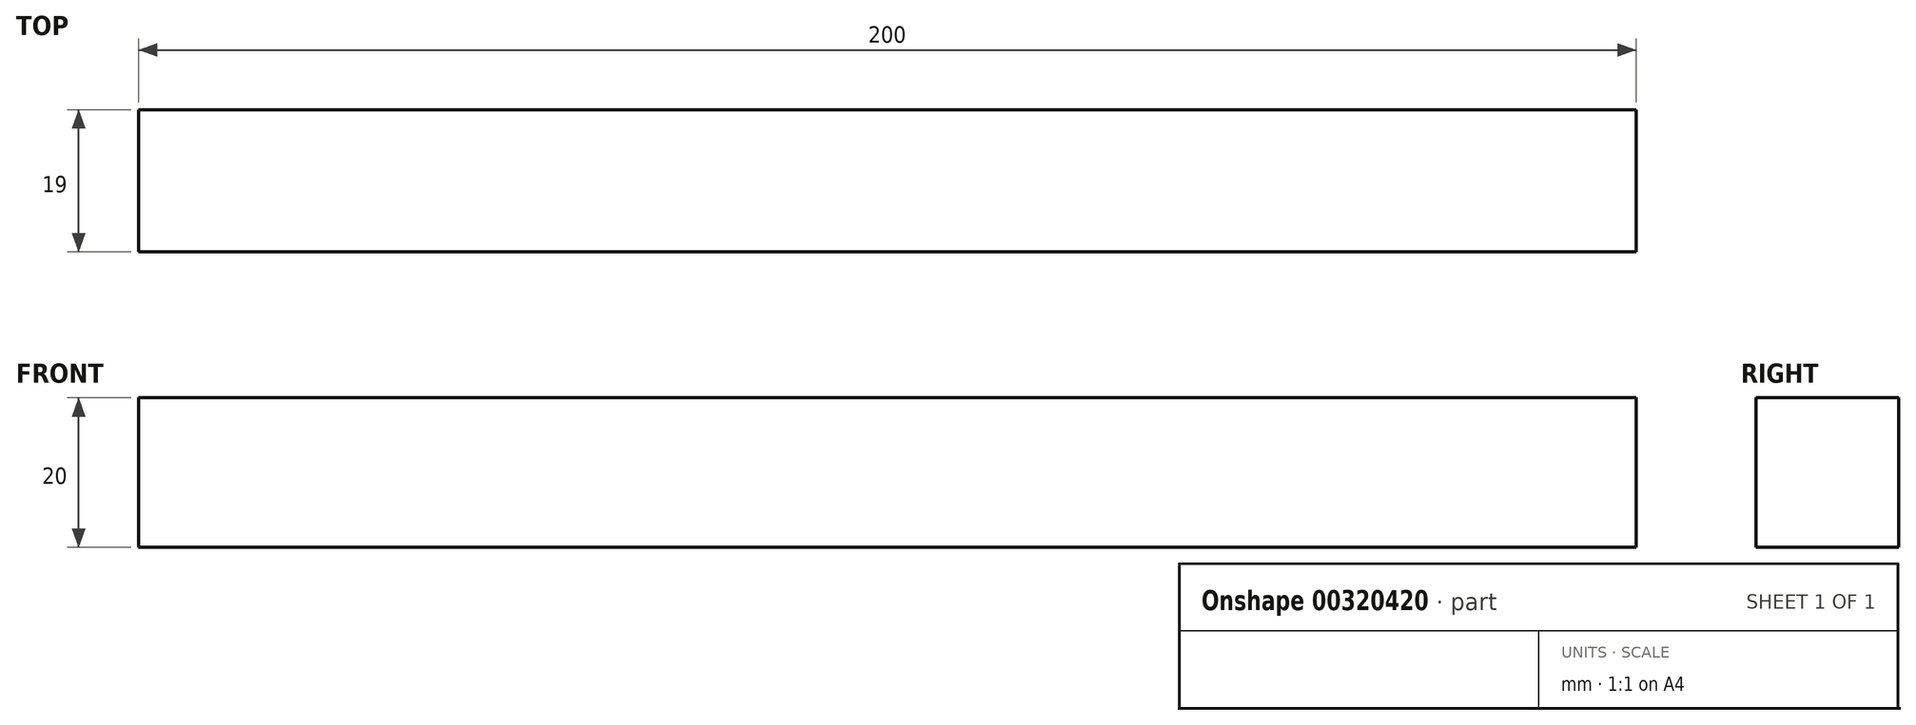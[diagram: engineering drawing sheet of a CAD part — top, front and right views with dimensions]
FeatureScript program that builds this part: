
annotation { "Feature Type Name" : "Feature", "Feature Type Description" : "" }
export const myFeature = defineFeature(function(context is Context, id is Id, definition is map)
    precondition{}
    {
        {
            var Q0;
            Q0=qCreatedBy(makeId("Front.planeOp"),FACE);
            var sketch = newSketch(context, id + "F0", { "sketchPlane" : qUnion([Q0])});
            skLineSegment(sketch, "E0.bottom", {"start": v(0, 0) * mm, "end": v(200, 0) * mm});
            skLineSegment(sketch, "E0.top", {"start": v(0, 20) * mm, "end": v(200, 20) * mm});
            skLineSegment(sketch, "E0.left", {"start": v(0, 0) * mm, "end": v(0, 20) * mm});
            skLineSegment(sketch, "E0.right", {"start": v(200, 0) * mm, "end": v(200, 20) * mm});
            skSolve(sketch);
        }
        {
            var Q0;
            Q0=makeQuery(id+"F0.imprint","IMPRINT",FACE,{"disambiguationData":[TD([[makeQuery(id+"F0.imprint","IMPRINT",EDGE,{"derivedFrom":sQuery(id+"F0.wireOp",EDGE,"E0.bottom")}),1.0]])]});
            extrude(context, id + "F1", {"entities" : qUnion([Q0]), "depth" : 19 * mm});
        }
    });
